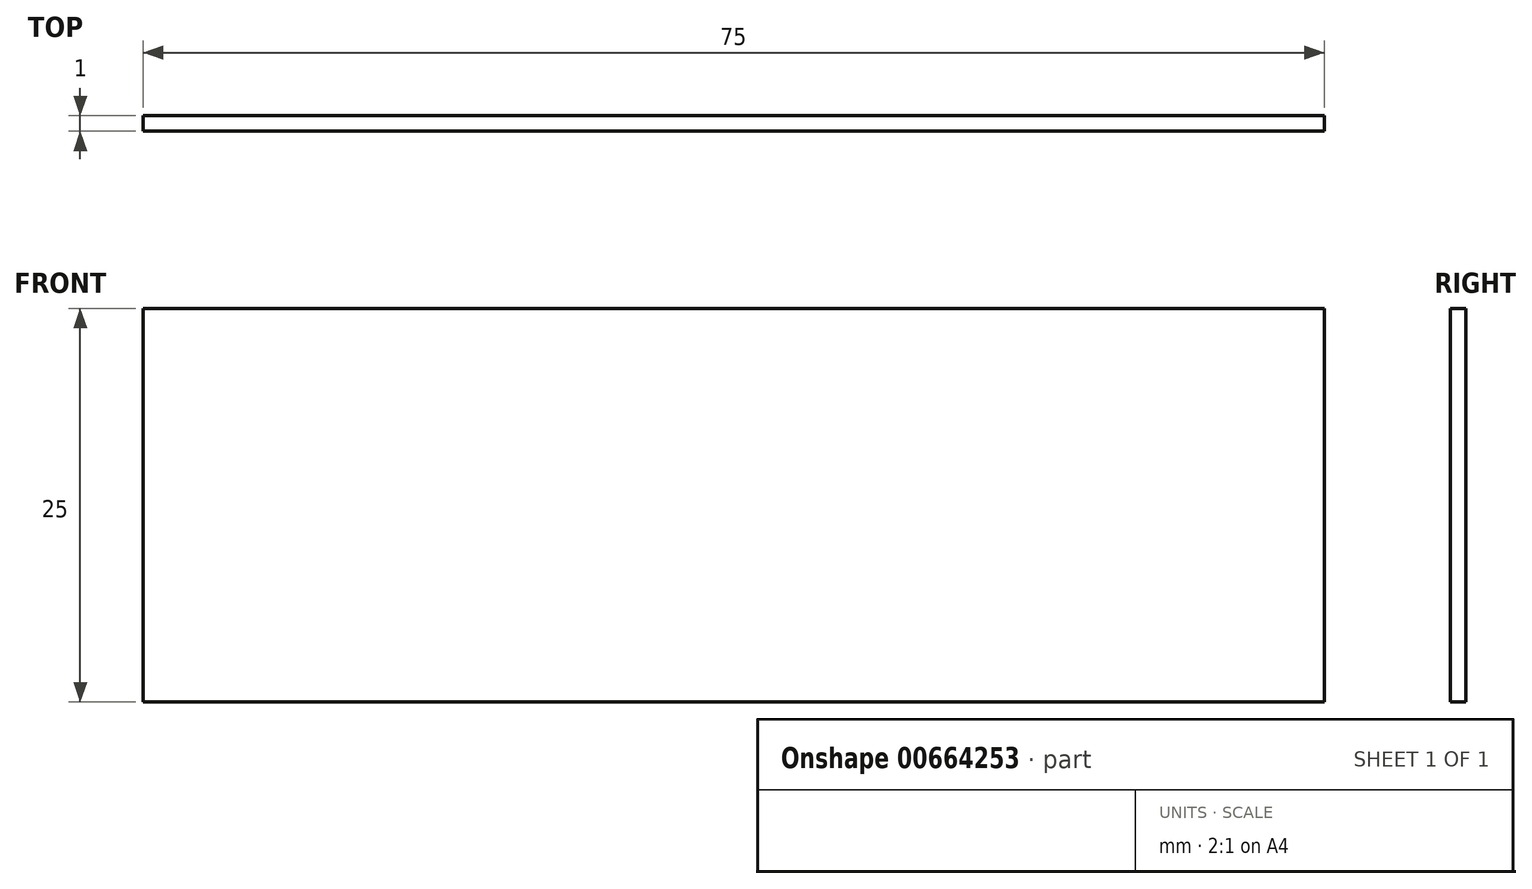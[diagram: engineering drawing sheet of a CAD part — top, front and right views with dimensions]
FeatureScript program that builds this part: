
annotation { "Feature Type Name" : "Feature", "Feature Type Description" : "" }
export const myFeature = defineFeature(function(context is Context, id is Id, definition is map)
    precondition{}
    {
        {
            var Q0;
            Q0=qCreatedBy(makeId("Front.planeOp"),FACE);
            var sketch = newSketch(context, id + "F0", { "sketchPlane" : qUnion([Q0])});
            skLineSegment(sketch, "E0.bottom", {"start": v(37.5, 12.5) * mm, "end": v(-37.5, 12.5) * mm});
            skLineSegment(sketch, "E0.top", {"start": v(37.5, -12.5) * mm, "end": v(-37.5, -12.5) * mm});
            skLineSegment(sketch, "E0.left", {"start": v(37.5, 12.5) * mm, "end": v(37.5, -12.5) * mm});
            skLineSegment(sketch, "E0.right", {"start": v(-37.5, 12.5) * mm, "end": v(-37.5, -12.5) * mm});
            skPoint(sketch, "E0.middle", {"position": v(0, 0) * mm});
            skSolve(sketch);
        }
        {
            var Q0;
            Q0=makeQuery(id+"F0.imprint","IMPRINT",FACE,{"disambiguationData":[TD([[makeQuery(id+"F0.imprint","IMPRINT",EDGE,{"derivedFrom":sQuery(id+"F0.wireOp",EDGE,"E0.bottom")}),1.0]])]});
            extrude(context, id + "F1", {"entities" : qUnion([Q0]), "depth" : 1 * mm, "offsetDistance" : 25 * mm});
        }
    });
